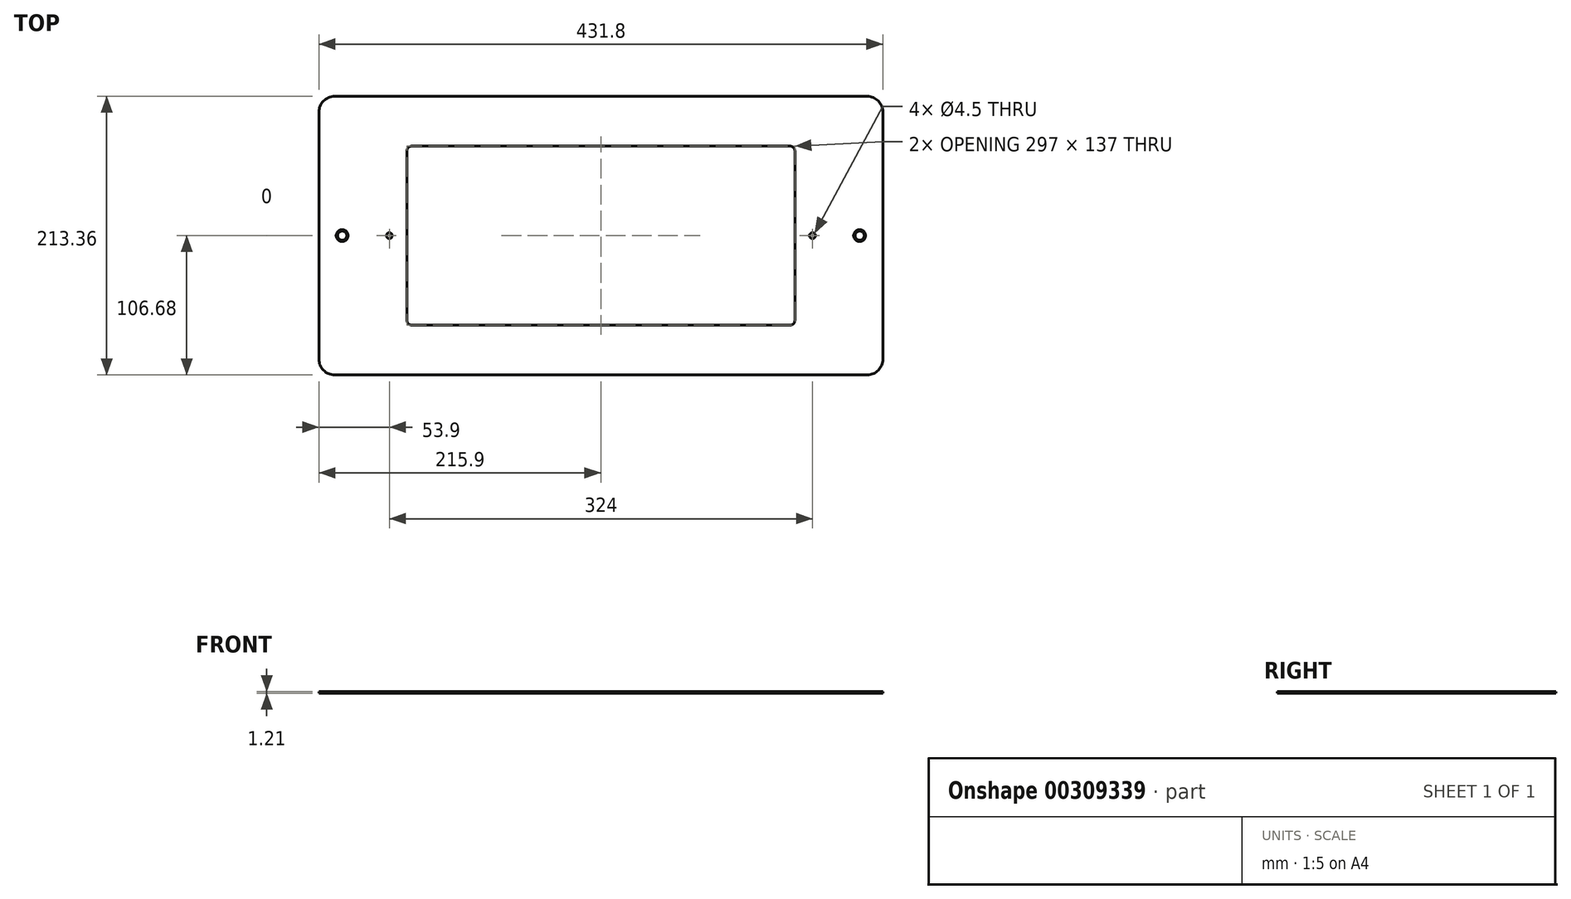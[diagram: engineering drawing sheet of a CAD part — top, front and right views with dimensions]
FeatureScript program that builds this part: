
annotation { "Feature Type Name" : "Feature", "Feature Type Description" : "" }
export const myFeature = defineFeature(function(context is Context, id is Id, definition is map)
    precondition{}
    {
        {
            var Q0;
            Q0=qCreatedBy(makeId("Top.planeOp"),FACE);
            var sketch = newSketch(context, id + "F0", { "sketchPlane" : qUnion([Q0])});
            skLineSegment(sketch, "E0.bottom", {"start": v(-145, 68.5) * mm, "end": v(145, 68.5) * mm});
            skLineSegment(sketch, "E0.top", {"start": v(-145, -68.5) * mm, "end": v(145, -68.5) * mm});
            skLineSegment(sketch, "E0.left", {"start": v(-148.5, 65) * mm, "end": v(-148.5, -65) * mm});
            skLineSegment(sketch, "E0.right", {"start": v(148.5, 65) * mm, "end": v(148.5, -65) * mm});
            skPoint(sketch, "E0.middle", {"position": v(0, 0) * mm});
            skLineSegment(sketch, "E1.bottom", {"start": v(-203.9, 106.68) * mm, "end": v(203.9, 106.68) * mm});
            skLineSegment(sketch, "E1.top", {"start": v(-203.9, -106.68) * mm, "end": v(203.9, -106.68) * mm});
            skLineSegment(sketch, "E1.left", {"start": v(-215.9, 94.68) * mm, "end": v(-215.9, -94.68) * mm});
            skLineSegment(sketch, "E1.right", {"start": v(215.9, 94.68) * mm, "end": v(215.9, -94.68) * mm});
            skPoint(sketch, "E2.visualSharp", {"position": v(-215.9, 106.68) * mm});
            skArc(sketch, "E2.filletArc", {"start": v(-203.9, 106.68) * mm, "mid": v(-212.39, 103.17) * mm, "end": v(-215.9, 94.68) * mm});
            skPoint(sketch, "E3.visualSharp", {"position": v(-215.9, -106.68) * mm});
            skArc(sketch, "E3.filletArc", {"start": v(-215.9, -94.68) * mm, "mid": v(-212.39, -103.17) * mm, "end": v(-203.9, -106.68) * mm});
            skPoint(sketch, "E4.visualSharp", {"position": v(215.9, 106.68) * mm});
            skArc(sketch, "E4.filletArc", {"start": v(215.9, 94.68) * mm, "mid": v(212.39, 103.17) * mm, "end": v(203.9, 106.68) * mm});
            skPoint(sketch, "E5.visualSharp", {"position": v(215.9, -106.68) * mm});
            skArc(sketch, "E5.filletArc", {"start": v(203.9, -106.68) * mm, "mid": v(212.39, -103.17) * mm, "end": v(215.9, -94.68) * mm});
            skPoint(sketch, "E6.visualSharp", {"position": v(148.5, 68.5) * mm});
            skArc(sketch, "E6.filletArc", {"start": v(148.5, 65) * mm, "mid": v(147.47, 67.47) * mm, "end": v(145, 68.5) * mm});
            skPoint(sketch, "E7.visualSharp", {"position": v(148.5, -68.5) * mm});
            skArc(sketch, "E7.filletArc", {"start": v(145, -68.5) * mm, "mid": v(147.47, -67.47) * mm, "end": v(148.5, -65) * mm});
            skPoint(sketch, "E8.visualSharp", {"position": v(-148.5, -68.5) * mm});
            skArc(sketch, "E8.filletArc", {"start": v(-148.5, -65) * mm, "mid": v(-147.47, -67.47) * mm, "end": v(-145, -68.5) * mm});
            skPoint(sketch, "E9.visualSharp", {"position": v(-148.5, 68.5) * mm});
            skArc(sketch, "E9.filletArc", {"start": v(-145, 68.5) * mm, "mid": v(-147.47, 67.47) * mm, "end": v(-148.5, 65) * mm});
            skSolve(sketch);
        }
        {
            var Q0;
            Q0 = qSketchRegion(id + "F0", true);
            extrude(context, id + "F1", {"entities" : qUnion([Q0]), "depth" : 1.21 * mm});
        }
        {
            var Q0;
            Q0=makeQuery(id+"F1.opExtrude","CAP_FACE",FACE,{"disambiguationData":[OSD([sQuery(id+"F0.wireOp",EDGE,"E0.bottom"),sQuery(id+"F0.wireOp",EDGE,"E0.top"),sQuery(id+"F0.wireOp",EDGE,"E0.left"),sQuery(id+"F0.wireOp",EDGE,"E0.right"),sQuery(id+"F0.wireOp",EDGE,"E1.bottom"),sQuery(id+"F0.wireOp",EDGE,"E1.top"),sQuery(id+"F0.wireOp",EDGE,"E1.left"),sQuery(id+"F0.wireOp",EDGE,"E1.right"),sQuery(id+"F0.wireOp",EDGE,"E2.filletArc"),sQuery(id+"F0.wireOp",EDGE,"E3.filletArc"),sQuery(id+"F0.wireOp",EDGE,"E4.filletArc"),sQuery(id+"F0.wireOp",EDGE,"E5.filletArc"),sQuery(id+"F0.wireOp",EDGE,"E6.filletArc"),sQuery(id+"F0.wireOp",EDGE,"E7.filletArc"),sQuery(id+"F0.wireOp",EDGE,"E8.filletArc"),sQuery(id+"F0.wireOp",EDGE,"E9.filletArc")])],"isStart":false});
            var sketch = newSketch(context, id + "F2", { "sketchPlane" : qUnion([Q0])});
            skPoint(sketch, "E10", {"position": v(-162, 0) * mm});
            skPoint(sketch, "E11", {"position": v(-198.12, 0) * mm});
            skPoint(sketch, "E12.MirrorP", {"position": v(162, 0) * mm});
            skPoint(sketch, "E13.MirrorP", {"position": v(198.12, 0) * mm});
            skSolve(sketch);
        }
        {
            var Q0;
            Q0=sQuery(id+"F2.wireOp",VERTEX,"E10");
            var Q1;
            Q1=sQuery(id+"F2.wireOp",VERTEX,"E12.MirrorP");
            var Q2;
            Q2=makeQuery(id+"F1.opExtrude","SWEPT_BODY",BODY,{"disambiguationData":[OSD([sQuery(id+"F0.wireOp",EDGE,"E0.bottom"),sQuery(id+"F0.wireOp",EDGE,"E0.top"),sQuery(id+"F0.wireOp",EDGE,"E0.left"),sQuery(id+"F0.wireOp",EDGE,"E0.right"),sQuery(id+"F0.wireOp",EDGE,"E1.bottom"),sQuery(id+"F0.wireOp",EDGE,"E1.top"),sQuery(id+"F0.wireOp",EDGE,"E1.left"),sQuery(id+"F0.wireOp",EDGE,"E1.right"),sQuery(id+"F0.wireOp",EDGE,"E2.filletArc"),sQuery(id+"F0.wireOp",EDGE,"E3.filletArc"),sQuery(id+"F0.wireOp",EDGE,"E4.filletArc"),sQuery(id+"F0.wireOp",EDGE,"E5.filletArc"),sQuery(id+"F0.wireOp",EDGE,"E6.filletArc"),sQuery(id+"F0.wireOp",EDGE,"E7.filletArc"),sQuery(id+"F0.wireOp",EDGE,"E8.filletArc"),sQuery(id+"F0.wireOp",EDGE,"E9.filletArc")])]});
            hole(context, id + "F3", {"style" : HoleStyle.SIMPLE, "endStyle" : HoleEndStyle.THROUGH, "standardTappedOrClearance" : lookupTablePath({ "standard" : "ANSI", "fit" : "Normal (ASME)", "size" : "#8", "type" : "Clearance" }), "standardBlindInLast" : lookupTablePath({ "fit" : "Free", "standard" : "ANSI", "size" : "#8", "type" : "Clearance" }), "holeDiameter" : 4.5 * mm, "tappedDepth" : 12.7 * mm, "tapClearance" : 3, "locations" : qUnion([Q0, Q1]), "scope" : qUnion([Q2])});
        }
        {
            var Q0;
            Q0=sQuery(id+"F2.wireOp",VERTEX,"E11");
            var Q1;
            Q1=sQuery(id+"F2.wireOp",VERTEX,"E13.MirrorP");
            var Q2;
            Q2=makeQuery(id+"F1.opExtrude","SWEPT_BODY",BODY,{"disambiguationData":[OSD([sQuery(id+"F0.wireOp",EDGE,"E0.bottom"),sQuery(id+"F0.wireOp",EDGE,"E0.top"),sQuery(id+"F0.wireOp",EDGE,"E0.left"),sQuery(id+"F0.wireOp",EDGE,"E0.right"),sQuery(id+"F0.wireOp",EDGE,"E1.bottom"),sQuery(id+"F0.wireOp",EDGE,"E1.top"),sQuery(id+"F0.wireOp",EDGE,"E1.left"),sQuery(id+"F0.wireOp",EDGE,"E1.right"),sQuery(id+"F0.wireOp",EDGE,"E2.filletArc"),sQuery(id+"F0.wireOp",EDGE,"E3.filletArc"),sQuery(id+"F0.wireOp",EDGE,"E4.filletArc"),sQuery(id+"F0.wireOp",EDGE,"E5.filletArc"),sQuery(id+"F0.wireOp",EDGE,"E6.filletArc"),sQuery(id+"F0.wireOp",EDGE,"E7.filletArc"),sQuery(id+"F0.wireOp",EDGE,"E8.filletArc"),sQuery(id+"F0.wireOp",EDGE,"E9.filletArc")])]});
            hole(context, id + "F4", {"style" : HoleStyle.C_SINK, "endStyle" : HoleEndStyle.THROUGH, "standardTappedOrClearance" : lookupTablePath({ "standard" : "ANSI", "fit" : "Close", "size" : "#8", "type" : "Clearance" }), "standardBlindInLast" : lookupTablePath({ "fit" : "Close", "standard" : "ANSI", "size" : "#8", "type" : "Clearance" }), "holeDiameter" : 4.32 * mm, "cSinkDiameter" : 9.12 * mm, "cSinkAngle" : 82 * degree, "tappedDepth" : 12.7 * mm, "tapClearance" : 3, "locations" : qUnion([Q0, Q1]), "scope" : qUnion([Q2])});
        }
        {
            var Q0;
            Q0=makeQuery(id+"F1.opExtrude","SWEPT_BODY",BODY,{"disambiguationData":[OSD([sQuery(id+"F0.wireOp",EDGE,"E0.bottom"),sQuery(id+"F0.wireOp",EDGE,"E0.top"),sQuery(id+"F0.wireOp",EDGE,"E0.left"),sQuery(id+"F0.wireOp",EDGE,"E0.right"),sQuery(id+"F0.wireOp",EDGE,"E1.bottom"),sQuery(id+"F0.wireOp",EDGE,"E1.top"),sQuery(id+"F0.wireOp",EDGE,"E1.left"),sQuery(id+"F0.wireOp",EDGE,"E1.right"),sQuery(id+"F0.wireOp",EDGE,"E2.filletArc"),sQuery(id+"F0.wireOp",EDGE,"E3.filletArc"),sQuery(id+"F0.wireOp",EDGE,"E4.filletArc"),sQuery(id+"F0.wireOp",EDGE,"E5.filletArc"),sQuery(id+"F0.wireOp",EDGE,"E6.filletArc"),sQuery(id+"F0.wireOp",EDGE,"E7.filletArc"),sQuery(id+"F0.wireOp",EDGE,"E8.filletArc"),sQuery(id+"F0.wireOp",EDGE,"E9.filletArc")])]});
            transform(context, id + "F5", {"entities" : qUnion([Q0]), "transformType" : TransformType.TRANSLATION_3D, "dx" : 0 * mm, "dy" : 0 * mm, "dz" : 0 * mm, "makeCopy" : true});
        }
    });
